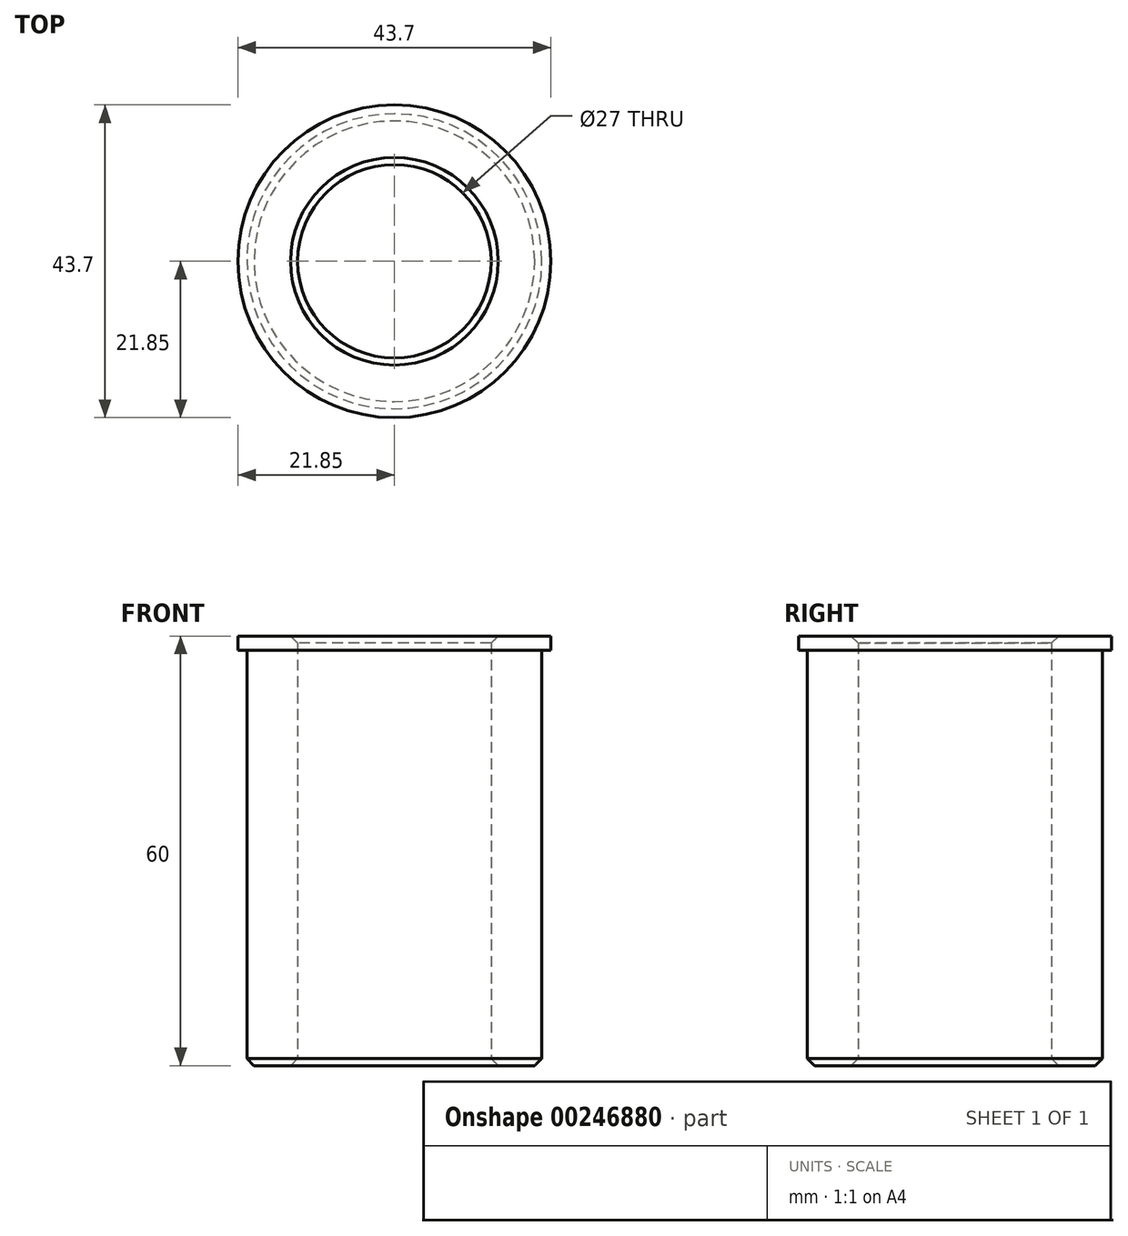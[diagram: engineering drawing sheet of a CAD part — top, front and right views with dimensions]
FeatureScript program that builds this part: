
annotation { "Feature Type Name" : "Feature", "Feature Type Description" : "" }
export const myFeature = defineFeature(function(context is Context, id is Id, definition is map)
    precondition{}
    {
        {
            var Q0;
            Q0=qCreatedBy(makeId("Top.planeOp"),FACE);
            var sketch = newSketch(context, id + "F0", { "sketchPlane" : qUnion([Q0])});
            skCircle(sketch, "E0", {"center": v(0, 0) * mm, "radius": 12.5 * mm});
            skCircle(sketch, "E1.0", {"center": v(0, 0) * mm, "radius": 13.5 * mm});
            skCircle(sketch, "E2", {"center": v(0, 0) * mm, "radius": 21.85 * mm});
            skCircle(sketch, "E3", {"center": v(0, 0) * mm, "radius": 15 * mm});
            skCircle(sketch, "E4", {"center": v(0, 0) * mm, "radius": 20.6 * mm});
            skSolve(sketch);
        }
        {
            var Q0;
            Q0=makeQuery(id+"F0.imprint","IMPRINT",FACE,{"disambiguationData":[TD([[makeQuery(id+"F0.imprint","IMPRINT",EDGE,{"derivedFrom":sQuery(id+"F0.wireOp",EDGE,"E2")}),1.0]])]});
            var Q1;
            Q1=makeQuery(id+"F0.imprint","IMPRINT",FACE,{"disambiguationData":[TD([[makeQuery(id+"F0.imprint","IMPRINT",EDGE,{"derivedFrom":sQuery(id+"F0.wireOp",EDGE,"E3")}),-1.0]])]});
            var Q2;
            Q2=makeQuery(id+"F0.imprint","IMPRINT",FACE,{"disambiguationData":[TD([[makeQuery(id+"F0.imprint","IMPRINT",EDGE,{"derivedFrom":sQuery(id+"F0.wireOp",EDGE,"E1.0")}),-1.0]])]});
            extrude(context, id + "F1", {"entities" : qUnion([Q0, Q1, Q2]), "depth" : 2 * mm});
        }
        {
            var Q0;
            Q0=makeQuery(id+"F0.imprint","IMPRINT",FACE,{"disambiguationData":[TD([[makeQuery(id+"F0.imprint","IMPRINT",EDGE,{"derivedFrom":sQuery(id+"F0.wireOp",EDGE,"E3")}),-1.0]])]});
            var Q1;
            Q1=makeQuery(id+"F0.imprint","IMPRINT",FACE,{"disambiguationData":[TD([[makeQuery(id+"F0.imprint","IMPRINT",EDGE,{"derivedFrom":sQuery(id+"F0.wireOp",EDGE,"E1.0")}),-1.0]])]});
            extrude(context, id + "F2", {"entities" : qUnion([Q0, Q1]), "operationType" : NewBodyOperationType.ADD, "oppositeDirection" : true, "depth" : 58 * mm});
        }
        {
            var Q0;
            Q0=makeQuery(id+"F2.opExtrude","CAP_EDGE",EDGE,{"disambiguationData":[OSD([sQuery(id+"F0.wireOp",EDGE,"E4")])],"isStart":false});
            var Q1;
            Q1=makeQuery(id+"F2.opExtrude","CAP_EDGE",EDGE,{"disambiguationData":[OSD([sQuery(id+"F0.wireOp",EDGE,"E1.0")])],"isStart":false});
            var Q2;
            Q2=makeQuery(id+"F1.opExtrude","CAP_EDGE",EDGE,{"disambiguationData":[OSD([sQuery(id+"F0.wireOp",EDGE,"E1.0")])],"isStart":false});
            chamfer(context, id + "F3", {"entities" : qUnion([Q0, Q1, Q2]), "width" : 1 * mm, "tangentPropagation" : true});
        }
    });
